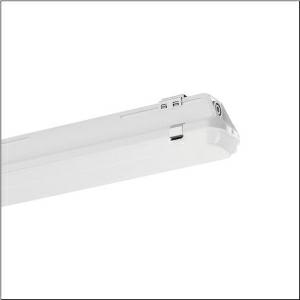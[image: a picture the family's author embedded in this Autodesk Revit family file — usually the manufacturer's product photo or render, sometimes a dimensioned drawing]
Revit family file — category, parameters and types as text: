
# Revit family: monsun_r__12_51fp10dp660h_aca9
name_source: partatom
category: Lighting Fixtures
units: mm (PartAtom-declared; Revit-internal decimal feet)

## family parameters
Cut with Voids When Loaded = No
Host = Face
Light Source = No
Part Type = Normal
Room Calculation Point = No
Round Connector Dimension = Use Diameter
Shared = No

## types (1)
- --- (1 x LED, 5970 lm, 34.6 W, 6500K)
    Apparent Load = 35 VA
    CIE Flux Codes = 47 77 93 94 100
    Color Rendering = 80
    Color Temperature = 6500K
    Default Elevation = 1800 mm
    Description = Monsun® 12, damp-proof luminaire, chain hanger, primary optical cover: enclosure, of PMMA, light emission: direct distribution, primary light characteristic: symmetric, installation type: suspended mounting, surface-mounted, horizontal mounting, vertical mounting, LED rated luminous flux: 5.970 lm, light colour: 865, colour temperature: 6500K, control gear: ECG DALI, with terminal, 5-pole, max. 2.5mm², mains connection: 220..240V, AC, 50/60Hz, rated input power: 35W, luminaire housing, of glass-fibre reinforced polyester, uncoated, bright grey, length: 1.590 mm, width: 90 mm, height: 88mm, clip for enclosure, of stainless steel (V2A), ceiling mounting element, of stainless steel (V2A), chain hanger, of stainless steel (V2A), protection rating (complete): IP66, insulation class (complete): insulation class I (protective earthing), certification: CE, ENEC, VDE, protection symbol: D, impact resistance: IK04, permissible ambient temperature for indoor applications: -25..+40°C, standard: EN 50419, EN 60598-2-1, no direct snow, no direct sun, no direct rain, for indoor or canopied outdoor use, corresponds to IFS (International Featured Standards) requirements for safety and quality in the food industry, for animal farming (ammonia tested): for use in cowhouse, pig house, horse-stables... (not for use in poultry stables), AT max for animal farming = 40°C, packaging unit: 1 piece
    Height = 89 mm
    Lamp = 1 x LED
    Lamp Light Flux = 5970 lm
    Lamp Power = 34.6 W
    Lamp count = 1
    Length = 1590 mm
    Luminous efficacy = 173 lm/W
    Manufacturer = Siteco
    ModVariant = No
    Model = 51FP10DP660H
    Mounting Place = Ceiling
    Mounting Type = Pendant
    Number of Poles = 1
    OnlyDefault = Yes
    Power Factor = 1
    Product Name = Monsun® 12
    Product group = damp-proof luminaire | ceiling pendant
    ProductGroupID = 908
    Protection Class = Protection class I
    Protection Degree = IP 66
    RLX_Detail_Level = 1
    RlxData = <blob elided: 92437 chars, md5=de04dbc1>
    Socket = socket
    Standby Power = 0 W
    System Light Flux = 5970 lm
    System Power = 35 W
    Type Comments = factory setting: luminous flux: 100 % | dim-lin: 254 | 232 mA
    Type Image = l_1004748.jpg
    URL = http://relux.com
    VarID = @adj_136171
    Voltage = 0 V
    Weight = 0.00 kg
    Width = 90 mm

## geometry (parser evidence)
native form markers: Blend x4, Sweep x14
no freeform markers — native parametric forms only
